# Revit family: Legrand XL³-S 160 encastré
name_source: partatom
category: Equipement électrique
units: mm (PartAtom-declared; Revit-internal decimal feet)

## family parameters
Basée sur le plan de construction = Non
Configuration du panneau = Deux colonnes, circuits au sein
Cote de connecteur circulaire = Utiliser le diamètre
Couper avec des vides une fois chargée = Non
Numéro OmniClass = 23.80.30.11.17
Partagée = Non
Point de calcul de pièce = Non
Titre OmniClass = Distribution Boards and Control Panels
Toujours verticalement = Oui
Type d'élément = Tableau de raccordement

## types (12) — shared parameters
Conditions Générale d'Utilisation = https://export.legrand.com
ETIM Class 6.0 = EC000261
Fabricant = Legrand
IK = 07
IP = 40
Image du type = XL3S160_encastre_337224_p_231245.jpg
Matière = Acier
Poids = 0.00 kg
RAL = 9003
URL = www.legrand.fr
distance coté zone d'installation = 138 mm  [stored 0.452756 ft]
porte = Oui
profondeur = 138 mm  [stored 0.452756 ft]
profondeur Encastré = 116 mm  [stored 0.380577 ft]
zero-valued in all types: Elévation par défaut

## per-type parameters (varying)
- Enveloppe de distribution - XL³ S 160 - Coffret encastré - Métal - 24 modules - 2 rangées: Coffret 337222=Oui; Coffret 337223=Non; Coffret 337224=Non; Coffret 337225=Non; Coffret 337226=Non; Coffret 337227=Non; Coffret 337228=Non; Coffret 337234=Non; Coffret 337235=Non; Coffret 337236=Non; Coffret 337237=Non; Coffret 337238=Non; Description=337222  Enveloppe de distribution - XL³ S 160 - Coffret encastré - Métal - 24 modules - 2 rangées; Hauteur 1=512 mm  [stored 1.67979 ft]; Hauteur 2=440 mm  [stored 1.44357 ft]; Largeur=667 mm  [stored 2.18832 ft]; Largeur zone d'installation=943 mm  [stored 3.09383 ft]; distance avant zone d'installation=667 mm  [stored 2.18832 ft]; module (24 ou 36)=24; nombre rangée=2; porte 337252=Oui; porte 337253=Non; porte 337254=Non; porte 337255=Non; porte 337256=Non; porte 337257=Non; porte 337258=Non; porte 337264=Non; porte 337265=Non; porte 337266=Non; porte 337267=Non; porte 337268=Non; profondeur zone d'installation=805 mm  [stored 2.64108 ft]
- Enveloppe de distribution - XL³ S 160 - Coffret encastré - Métal - 24 modules - 3 rangées: Coffret 337222=Non; Coffret 337223=Oui; Coffret 337224=Non; Coffret 337225=Non; Coffret 337226=Non; Coffret 337227=Non; Coffret 337228=Non; Coffret 337234=Non; Coffret 337235=Non; Coffret 337236=Non; Coffret 337237=Non; Coffret 337238=Non; Description=337223  Enveloppe de distribution - XL³ S 160 - Coffret encastré - Métal - 24 modules - 3 rangées; Hauteur 1=662 mm  [stored 2.17192 ft]; Hauteur 2=590 mm  [stored 1.9357 ft]; Largeur=667 mm  [stored 2.18832 ft]; Largeur zone d'installation=943 mm  [stored 3.09383 ft]; distance avant zone d'installation=667 mm  [stored 2.18832 ft]; module (24 ou 36)=24; nombre rangée=3; porte 337252=Non; porte 337253=Oui; porte 337254=Non; porte 337255=Non; porte 337256=Non; porte 337257=Non; porte 337258=Non; porte 337264=Non; porte 337265=Non; porte 337266=Non; porte 337267=Non; porte 337268=Non; profondeur zone d'installation=805 mm  [stored 2.64108 ft]
- Enveloppe de distribution - XL³ S 160 - Coffret encastré - Métal - 24 modules - 4 rangées: Coffret 337222=Non; Coffret 337223=Non; Coffret 337224=Oui; Coffret 337225=Non; Coffret 337226=Non; Coffret 337227=Non; Coffret 337228=Non; Coffret 337234=Non; Coffret 337235=Non; Coffret 337236=Non; Coffret 337237=Non; Coffret 337238=Non; Description=337224  Enveloppe de distribution - XL³ S 160 - Coffret encastré - Métal - 24 modules - 4 rangées; Hauteur 1=812 mm  [stored 2.66404 ft]; Hauteur 2=740 mm  [stored 2.42782 ft]; Largeur=667 mm  [stored 2.18832 ft]; Largeur zone d'installation=943 mm  [stored 3.09383 ft]; distance avant zone d'installation=667 mm  [stored 2.18832 ft]; module (24 ou 36)=24; nombre rangée=4; porte 337252=Non; porte 337253=Non; porte 337254=Oui; porte 337255=Non; porte 337256=Non; porte 337257=Non; porte 337258=Non; porte 337264=Non; porte 337265=Non; porte 337266=Non; porte 337267=Non; porte 337268=Non; profondeur zone d'installation=805 mm  [stored 2.64108 ft]
- Enveloppe de distribution - XL³ S 160 - Coffret encastré - Métal - 24 modules - 5 rangées: Coffret 337222=Non; Coffret 337223=Non; Coffret 337224=Non; Coffret 337225=Oui; Coffret 337226=Non; Coffret 337227=Non; Coffret 337228=Non; Coffret 337234=Non; Coffret 337235=Non; Coffret 337236=Non; Coffret 337237=Non; Coffret 337238=Non; Description=337225  Enveloppe de distribution - XL³ S 160 - Coffret encastré - Métal - 24 modules - 5 rangées; Hauteur 1=962 mm  [stored 3.15617 ft]; Hauteur 2=890 mm  [stored 2.91995 ft]; Largeur=667 mm  [stored 2.18832 ft]; Largeur zone d'installation=943 mm  [stored 3.09383 ft]; distance avant zone d'installation=667 mm  [stored 2.18832 ft]; module (24 ou 36)=24; nombre rangée=5; porte 337252=Non; porte 337253=Non; porte 337254=Non; porte 337255=Oui; porte 337256=Non; porte 337257=Non; porte 337258=Non; porte 337264=Non; porte 337265=Non; porte 337266=Non; porte 337267=Non; porte 337268=Non; profondeur zone d'installation=805 mm  [stored 2.64108 ft]
- Enveloppe de distribution - XL³ S 160 - Coffret encastré - Métal - 24 modules - 6 rangées: Coffret 337222=Non; Coffret 337223=Non; Coffret 337224=Non; Coffret 337225=Non; Coffret 337226=Oui; Coffret 337227=Non; Coffret 337228=Non; Coffret 337234=Non; Coffret 337235=Non; Coffret 337236=Non; Coffret 337237=Non; Coffret 337238=Non; Description=337226  Enveloppe de distribution - XL³ S 160 - Coffret encastré - Métal - 24 modules - 6 rangées; Hauteur 1=1112 mm  [stored 3.64829 ft]; Hauteur 2=1040 mm  [stored 3.41207 ft]; Largeur=667 mm  [stored 2.18832 ft]; Largeur zone d'installation=943 mm  [stored 3.09383 ft]; distance avant zone d'installation=667 mm  [stored 2.18832 ft]; module (24 ou 36)=24; nombre rangée=6; porte 337252=Non; porte 337253=Non; porte 337254=Non; porte 337255=Non; porte 337256=Oui; porte 337257=Non; porte 337258=Non; porte 337264=Non; porte 337265=Non; porte 337266=Non; porte 337267=Non; porte 337268=Non; profondeur zone d'installation=805 mm  [stored 2.64108 ft]
- Enveloppe de distribution - XL³ S 160 - Coffret encastré - Métal - 24 modules - 7 rangées: Coffret 337222=Non; Coffret 337223=Non; Coffret 337224=Non; Coffret 337225=Non; Coffret 337226=Non; Coffret 337227=Oui; Coffret 337228=Non; Coffret 337234=Non; Coffret 337235=Non; Coffret 337236=Non; Coffret 337237=Non; Coffret 337238=Non; Description=337227  Enveloppe de distribution - XL³ S 160 - Coffret encastré - Métal - 24 modules - 7 rangées; Hauteur 1=1262 mm  [stored 4.14042 ft]; Hauteur 2=1190 mm  [stored 3.9042 ft]; Largeur=667 mm  [stored 2.18832 ft]; Largeur zone d'installation=943 mm  [stored 3.09383 ft]; distance avant zone d'installation=667 mm  [stored 2.18832 ft]; module (24 ou 36)=24; nombre rangée=7; porte 337252=Non; porte 337253=Non; porte 337254=Non; porte 337255=Non; porte 337256=Non; porte 337257=Oui; porte 337258=Non; porte 337264=Non; porte 337265=Non; porte 337266=Non; porte 337267=Non; porte 337268=Non; profondeur zone d'installation=805 mm  [stored 2.64108 ft]
- Enveloppe de distribution - XL³ S 160 - Coffret encastré - Métal - 24 modules - 8 rangées: Coffret 337222=Non; Coffret 337223=Non; Coffret 337224=Non; Coffret 337225=Non; Coffret 337226=Non; Coffret 337227=Non; Coffret 337228=Oui; Coffret 337234=Non; Coffret 337235=Non; Coffret 337236=Non; Coffret 337237=Non; Coffret 337238=Non; Description=337228  Enveloppe de distribution - XL³ S 160 - Coffret encastré - Métal - 24 modules - 8 rangées; Hauteur 1=1412 mm  [stored 4.63255 ft]; Hauteur 2=1340 mm  [stored 4.39633 ft]; Largeur=667 mm  [stored 2.18832 ft]; Largeur zone d'installation=943 mm  [stored 3.09383 ft]; distance avant zone d'installation=667 mm  [stored 2.18832 ft]; module (24 ou 36)=24; nombre rangée=8; porte 337252=Non; porte 337253=Non; porte 337254=Non; porte 337255=Non; porte 337256=Non; porte 337257=Non; porte 337258=Oui; porte 337264=Non; porte 337265=Non; porte 337266=Non; porte 337267=Non; porte 337268=Non; profondeur zone d'installation=805 mm  [stored 2.64108 ft]
- Enveloppe de distribution - XL³ S 160 - Coffret encastré - Métal - 36 modules - 4 rangées: Coffret 337222=Non; Coffret 337223=Non; Coffret 337224=Non; Coffret 337225=Non; Coffret 337226=Non; Coffret 337227=Non; Coffret 337228=Non; Coffret 337234=Oui; Coffret 337235=Non; Coffret 337236=Non; Coffret 337237=Non; Coffret 337238=Non; Description=337234  Enveloppe de distribution - XL³ S 160 - Coffret encastré - Métal - 36 modules - 4 rangées; Hauteur 1=812 mm  [stored 2.66404 ft]; Hauteur 2=740 mm  [stored 2.42782 ft]; Largeur=883 mm  [stored 2.89698 ft]; Largeur zone d'installation=1159 mm; distance avant zone d'installation=883 mm  [stored 2.89698 ft]; module (24 ou 36)=36; nombre rangée=4; porte 337252=Non; porte 337253=Non; porte 337254=Non; porte 337255=Non; porte 337256=Non; porte 337257=Non; porte 337258=Non; porte 337264=Oui; porte 337265=Non; porte 337266=Non; porte 337267=Non; porte 337268=Non; profondeur zone d'installation=1021 mm  [stored 3.34974 ft]
- Enveloppe de distribution - XL³ S 160 - Coffret encastré - Métal - 36 modules - 5 rangées: Coffret 337222=Non; Coffret 337223=Non; Coffret 337224=Non; Coffret 337225=Non; Coffret 337226=Non; Coffret 337227=Non; Coffret 337228=Non; Coffret 337234=Non; Coffret 337235=Oui; Coffret 337236=Non; Coffret 337237=Non; Coffret 337238=Non; Description=337235  Enveloppe de distribution - XL³ S 160 - Coffret encastré - Métal - 36 modules - 5 rangées; Hauteur 1=962 mm  [stored 3.15617 ft]; Hauteur 2=890 mm  [stored 2.91995 ft]; Largeur=883 mm  [stored 2.89698 ft]; Largeur zone d'installation=1159 mm; distance avant zone d'installation=883 mm  [stored 2.89698 ft]; module (24 ou 36)=36; nombre rangée=5; porte 337252=Non; porte 337253=Non; porte 337254=Non; porte 337255=Non; porte 337256=Non; porte 337257=Non; porte 337258=Non; porte 337264=Non; porte 337265=Oui; porte 337266=Non; porte 337267=Non; porte 337268=Non; profondeur zone d'installation=1021 mm  [stored 3.34974 ft]
- Enveloppe de distribution - XL³ S 160 - Coffret encastré - Métal - 36 modules - 6 rangées: Coffret 337222=Non; Coffret 337223=Non; Coffret 337224=Non; Coffret 337225=Non; Coffret 337226=Non; Coffret 337227=Non; Coffret 337228=Non; Coffret 337234=Non; Coffret 337235=Non; Coffret 337236=Oui; Coffret 337237=Non; Coffret 337238=Non; Description=337236  Enveloppe de distribution - XL³ S 160 - Coffret encastré - Métal - 36 modules - 6 rangées; Hauteur 1=1112 mm  [stored 3.64829 ft]; Hauteur 2=1040 mm  [stored 3.41207 ft]; Largeur=883 mm  [stored 2.89698 ft]; Largeur zone d'installation=1159 mm; distance avant zone d'installation=883 mm  [stored 2.89698 ft]; module (24 ou 36)=36; nombre rangée=6; porte 337252=Non; porte 337253=Non; porte 337254=Non; porte 337255=Non; porte 337256=Non; porte 337257=Non; porte 337258=Non; porte 337264=Non; porte 337265=Non; porte 337266=Oui; porte 337267=Non; porte 337268=Non; profondeur zone d'installation=1021 mm  [stored 3.34974 ft]
- Enveloppe de distribution - XL³ S 160 - Coffret encastré - Métal - 36 modules - 7 rangées: Coffret 337222=Non; Coffret 337223=Non; Coffret 337224=Non; Coffret 337225=Non; Coffret 337226=Non; Coffret 337227=Non; Coffret 337228=Non; Coffret 337234=Non; Coffret 337235=Non; Coffret 337236=Non; Coffret 337237=Oui; Coffret 337238=Non; Description=337237  Enveloppe de distribution - XL³ S 160 - Coffret encastré - Métal - 36 modules - 7 rangées; Hauteur 1=1262 mm  [stored 4.14042 ft]; Hauteur 2=1190 mm  [stored 3.9042 ft]; Largeur=883 mm  [stored 2.89698 ft]; Largeur zone d'installation=1159 mm; distance avant zone d'installation=883 mm  [stored 2.89698 ft]; module (24 ou 36)=36; nombre rangée=7; porte 337252=Non; porte 337253=Non; porte 337254=Non; porte 337255=Non; porte 337256=Non; porte 337257=Non; porte 337258=Non; porte 337264=Non; porte 337265=Non; porte 337266=Non; porte 337267=Oui; porte 337268=Non; profondeur zone d'installation=1021 mm  [stored 3.34974 ft]
- Enveloppe de distribution - XL³ S 160 - Coffret encastré - Métal - 36 modules - 8 rangées: Coffret 337222=Non; Coffret 337223=Non; Coffret 337224=Non; Coffret 337225=Non; Coffret 337226=Non; Coffret 337227=Non; Coffret 337228=Non; Coffret 337234=Non; Coffret 337235=Non; Coffret 337236=Non; Coffret 337237=Non; Coffret 337238=Oui; Description=337238  Enveloppe de distribution - XL³ S 160 - Coffret encastré - Métal - 36 modules - 8 rangées; Hauteur 1=1412 mm  [stored 4.63255 ft]; Hauteur 2=1340 mm  [stored 4.39633 ft]; Largeur=883 mm  [stored 2.89698 ft]; Largeur zone d'installation=1159 mm; distance avant zone d'installation=883 mm  [stored 2.89698 ft]; module (24 ou 36)=36; nombre rangée=8; porte 337252=Non; porte 337253=Non; porte 337254=Non; porte 337255=Non; porte 337256=Non; porte 337257=Non; porte 337258=Non; porte 337264=Non; porte 337265=Non; porte 337266=Non; porte 337267=Non; porte 337268=Oui; profondeur zone d'installation=1021 mm  [stored 3.34974 ft]

note: [stored X ft] marks values corroborated as IEEE doubles in the binary element streams (Revit-internal decimal feet)
